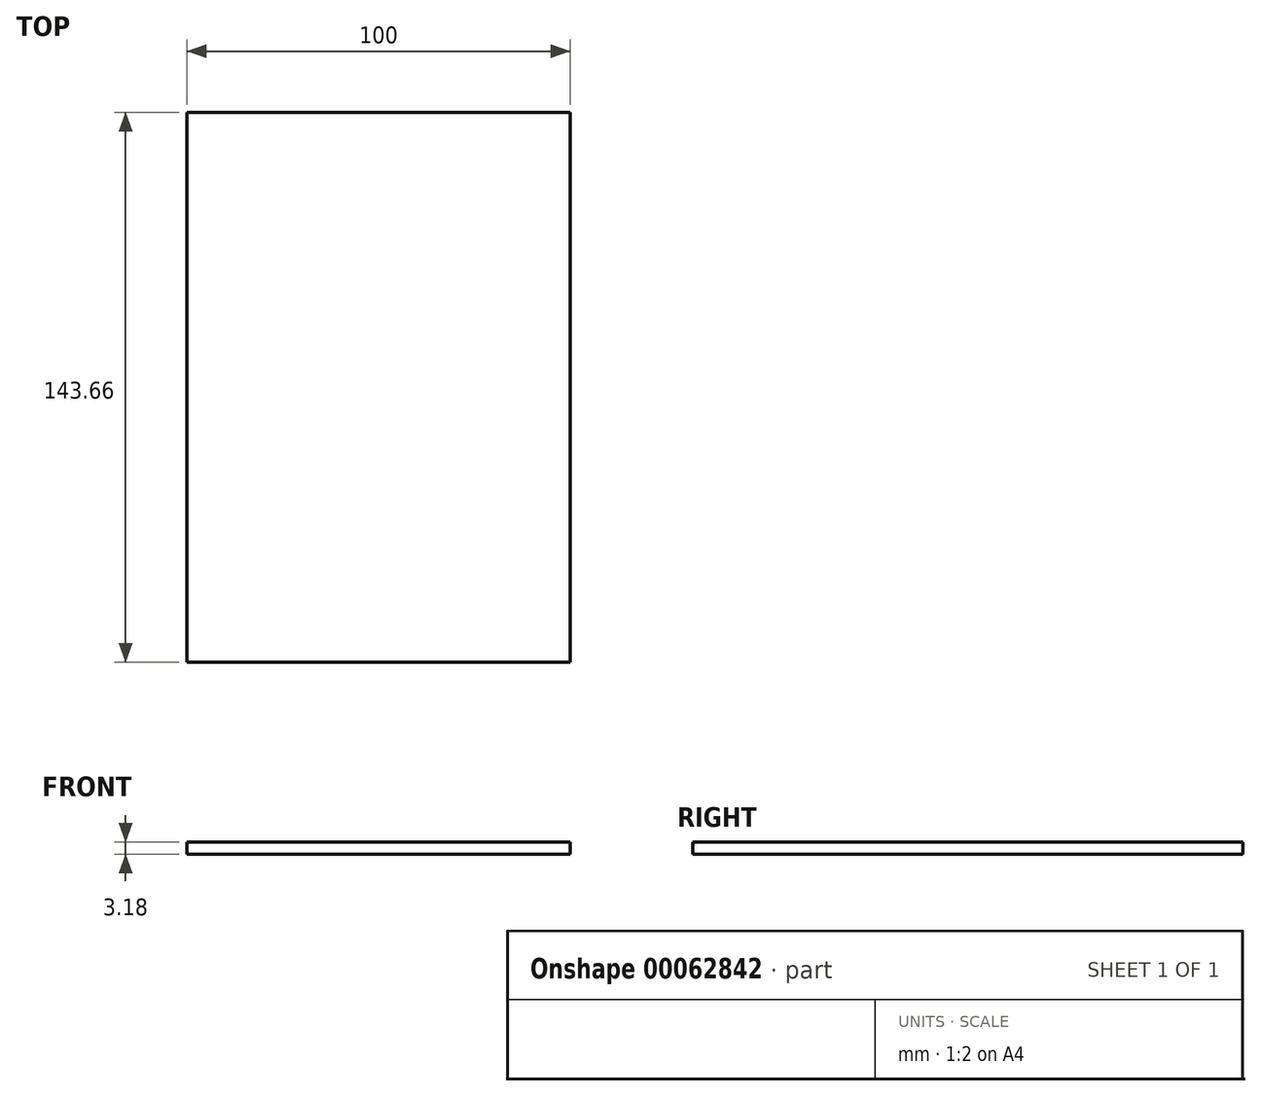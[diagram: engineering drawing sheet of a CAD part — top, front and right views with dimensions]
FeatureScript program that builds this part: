
annotation { "Feature Type Name" : "Feature", "Feature Type Description" : "" }
export const myFeature = defineFeature(function(context is Context, id is Id, definition is map)
    precondition{}
    {
        {
            var Q0;
            Q0=qCreatedBy(makeId("Top.planeOp"),FACE);
            var sketch = newSketch(context, id + "F0", { "sketchPlane" : qUnion([Q0])});
            skLineSegment(sketch, "E0.rect.bottom", {"start": v(-50, 71.82) * mm, "end": v(50, 71.82) * mm});
            skLineSegment(sketch, "E0.rect.top", {"start": v(-50, -71.83) * mm, "end": v(50, -71.83) * mm});
            skLineSegment(sketch, "E0.rect.left", {"start": v(-50, 71.82) * mm, "end": v(-50, -71.83) * mm});
            skLineSegment(sketch, "E0.rect.right", {"start": v(50, 71.82) * mm, "end": v(50, -71.83) * mm});
            skPoint(sketch, "E0.rect.middle", {"position": v(0, 0) * mm});
            skSolve(sketch);
        }
        {
            var Q0;
            Q0=makeQuery(id+"F0.imprint","IMPRINT",FACE,{"disambiguationData":[TD([[makeQuery(id+"F0.imprint","IMPRINT",EDGE,{"derivedFrom":sQuery(id+"F0.wireOp",EDGE,"E0.rect.bottom")}),-1.0]])]});
            extrude(context, id + "F1", {"entities" : qUnion([Q0]), "endBound" : BoundingType.SYMMETRIC, "depth" : 3.17 * mm});
        }
    });
